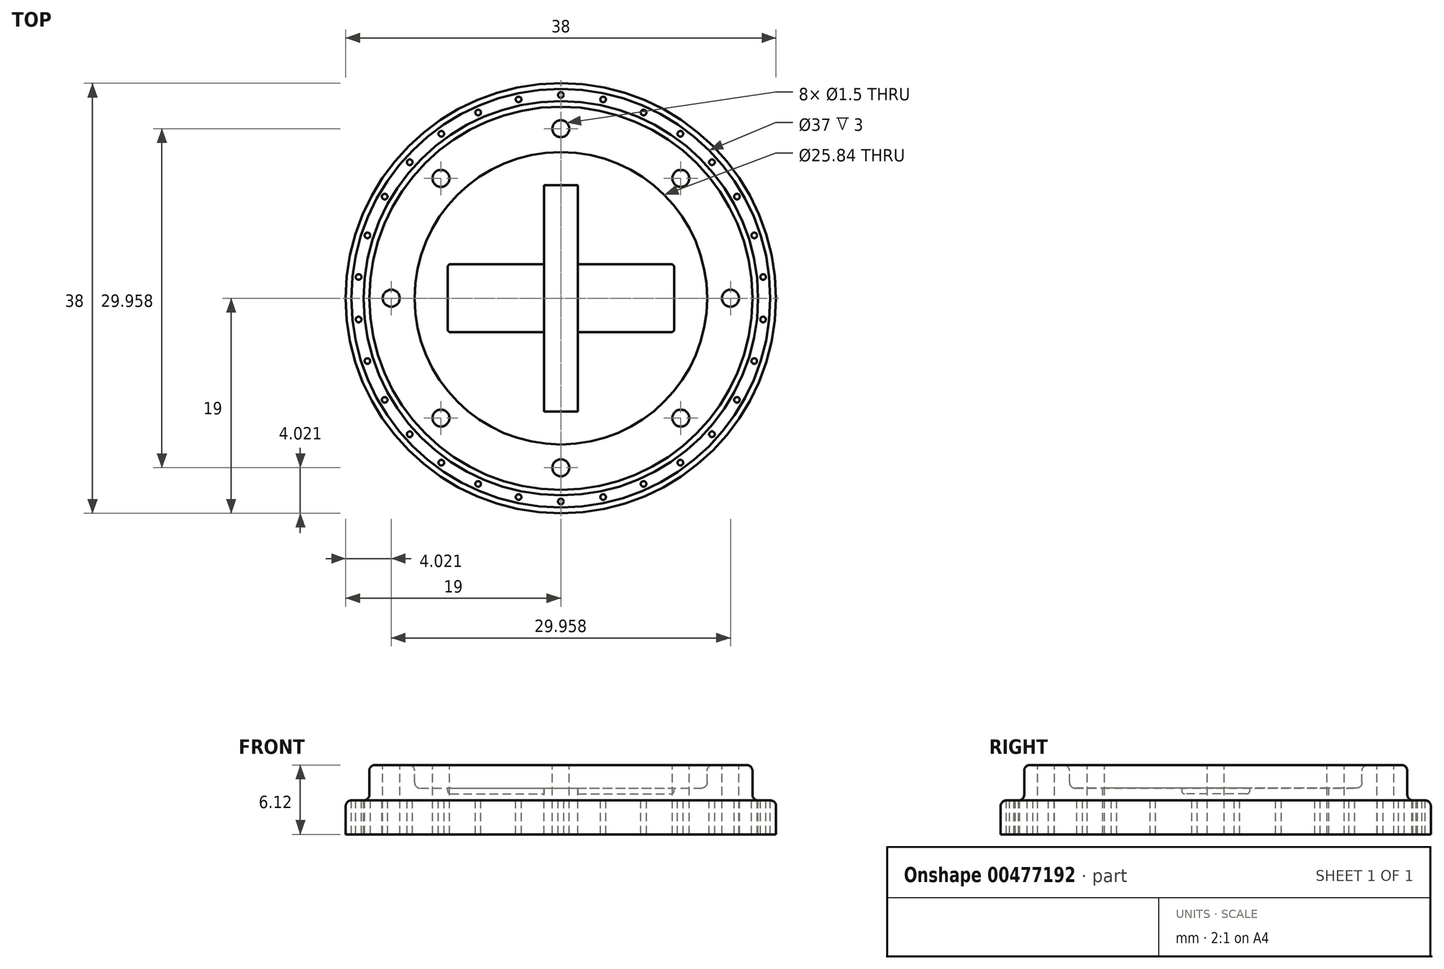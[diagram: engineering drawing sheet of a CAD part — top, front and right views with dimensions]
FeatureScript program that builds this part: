
annotation { "Feature Type Name" : "Feature", "Feature Type Description" : "" }
export const myFeature = defineFeature(function(context is Context, id is Id, definition is map)
    precondition{}
    {
        {
            var Q0;
            Q0=qCreatedBy(makeId("Front.planeOp"),FACE);
            var sketch = newSketch(context, id + "F0", { "sketchPlane" : qUnion([Q0])});
            skLineSegment(sketch, "E0", {"start": v(0, 0) * mm, "end": v(-19, 0) * mm});
            skLineSegment(sketch, "E1", {"start": v(-19, 0) * mm, "end": v(-19, 3) * mm});
            skLineSegment(sketch, "E2", {"start": v(-19, 3) * mm, "end": v(-16.92, 3) * mm});
            skLineSegment(sketch, "E3", {"start": v(-16.92, 3) * mm, "end": v(-16.92, 6.12) * mm});
            skLineSegment(sketch, "E4", {"start": v(-16.92, 6.12) * mm, "end": v(-12.92, 6.12) * mm});
            skLineSegment(sketch, "E5", {"start": v(-12.92, 6.12) * mm, "end": v(-12.92, 4.08) * mm});
            skLineSegment(sketch, "E6", {"start": v(-12.92, 4.08) * mm, "end": v(0, 4.08) * mm});
            skLineSegment(sketch, "E7", {"start": v(0, 4.08) * mm, "end": v(0, 0) * mm});
            skSolve(sketch);
        }
        {
            var Q0;
            Q0 = qSketchRegion(id + "F0", true);
            var Q1;
            Q1=sQuery(id+"F0.wireOp",EDGE,"E7");
            revolve(context, id + "F1", {"entities" : qUnion([Q0]), "axis" : qUnion([Q1]), "revolveType" : RevolveType.FULL});
        }
        {
            var Q0;
            Q0=makeQuery(id+"F1.opRevolve","SWEPT_EDGE",EDGE,{"disambiguationData":[OSD([sQuery(id+"F0.wireOp",EDGE,"E2"),sQuery(id+"F0.wireOp",EDGE,"E3")])]});
            var Q1;
            Q1=makeQuery(id+"F1.opRevolve","SWEPT_EDGE",EDGE,{"disambiguationData":[OSD([sQuery(id+"F0.wireOp",EDGE,"E1"),sQuery(id+"F0.wireOp",EDGE,"E2")])]});
            fillet(context, id + "F2", {"entities" : qUnion([Q0, Q1]), "radius" : 0.5 * mm, "tangentPropagation" : true, "allowEdgeOverflow" : false});
        }
        {
            var Q0;
            Q0=makeQuery(id+"F1.opRevolve","SWEPT_EDGE",EDGE,{"disambiguationData":[OSD([sQuery(id+"F0.wireOp",EDGE,"E3"),sQuery(id+"F0.wireOp",EDGE,"E4")])]});
            var Q1;
            Q1=makeQuery(id+"F1.opRevolve","SWEPT_EDGE",EDGE,{"disambiguationData":[OSD([sQuery(id+"F0.wireOp",EDGE,"E4"),sQuery(id+"F0.wireOp",EDGE,"E5")])]});
            var Q2;
            Q2=makeQuery(id+"F1.opRevolve","SWEPT_EDGE",EDGE,{"disambiguationData":[OSD([sQuery(id+"F0.wireOp",EDGE,"E5"),sQuery(id+"F0.wireOp",EDGE,"E6")])]});
            fillet(context, id + "F3", {"entities" : qUnion([Q0, Q1, Q2]), "radius" : 0.5 * mm, "tangentPropagation" : true, "allowEdgeOverflow" : false});
        }
        {
            var Q0;
            Q0=makeQuery(id+"F1.opRevolve","SWEPT_FACE",FACE,{"disambiguationData":[OSD([sQuery(id+"F0.wireOp",EDGE,"E6")])]});
            var Q1;
            Q1 = qBodyType(qCreatedBy(id + "F5" ,EDGE), BodyType.WIRE);
            cPlane(context, id + "F4", {"entities" : qUnion([Q0, Q1]), "cplaneType" : CPlaneType.OFFSET, "offset" : 0 * mm, "width" : 150 * mm, "height" : 150 * mm});
        }
        {
            var Q0;
            Q0=qCreatedBy(id+"F4.planeOp",FACE);
            var sketch = newSketch(context, id + "F5", { "sketchPlane" : qUnion([Q0])});
            skLineSegment(sketch, "E8.bottom", {"start": v(-10, 3) * mm, "end": v(10, 3) * mm});
            skLineSegment(sketch, "E8.top", {"start": v(-10, -3) * mm, "end": v(10, -3) * mm});
            skLineSegment(sketch, "E8.left", {"start": v(-10, 3) * mm, "end": v(-10, -3) * mm});
            skLineSegment(sketch, "E8.right", {"start": v(10, 3) * mm, "end": v(10, -3) * mm});
            skPoint(sketch, "E8.middle", {"position": v(0, 0) * mm});
            skSolve(sketch);
        }
        {
            var Q0;
            Q0 = qSketchRegion(id + "F5", true);
            extrude(context, id + "F6", {"entities" : qUnion([Q0]), "operationType" : NewBodyOperationType.REMOVE, "oppositeDirection" : true, "depth" : 0.5 * mm});
        }
        {
            var Q0;
            Q0=makeQuery(id+"F6.boolean.opBoolean","COPY",EDGE,{"derivedFrom":makeQuery(id+"F6.opExtrude","SWEPT_EDGE",EDGE,{"disambiguationData":[OSD([sQuery(id+"F5.wireOp",EDGE,"E8.bottom"),sQuery(id+"F5.wireOp",EDGE,"E8.left")])]})});
            var Q1;
            Q1=makeQuery(id+"F6.boolean.opBoolean","COPY",EDGE,{"derivedFrom":makeQuery(id+"F6.opExtrude","SWEPT_EDGE",EDGE,{"disambiguationData":[OSD([sQuery(id+"F5.wireOp",EDGE,"E8.top"),sQuery(id+"F5.wireOp",EDGE,"E8.left")])]})});
            var Q2;
            Q2=makeQuery(id+"F6.boolean.opBoolean","COPY",EDGE,{"derivedFrom":makeQuery(id+"F6.opExtrude","SWEPT_EDGE",EDGE,{"disambiguationData":[OSD([sQuery(id+"F5.wireOp",EDGE,"E8.bottom"),sQuery(id+"F5.wireOp",EDGE,"E8.right")])]})});
            var Q3;
            Q3=makeQuery(id+"F6.boolean.opBoolean","COPY",EDGE,{"derivedFrom":makeQuery(id+"F6.opExtrude","SWEPT_EDGE",EDGE,{"disambiguationData":[OSD([sQuery(id+"F5.wireOp",EDGE,"E8.top"),sQuery(id+"F5.wireOp",EDGE,"E8.right")])]})});
            var Q4;
            Q4=makeQuery(id+"F6.boolean.opBoolean","COPY",EDGE,{"derivedFrom":makeQuery(id+"F6.opExtrude","CAP_EDGE",EDGE,{"disambiguationData":[OSD([sQuery(id+"F5.wireOp",EDGE,"E8.right")])],"isStart":false})});
            var Q5;
            Q5=makeQuery(id+"F6.boolean.opBoolean","COPY",EDGE,{"derivedFrom":makeQuery(id+"F6.opExtrude","CAP_EDGE",EDGE,{"disambiguationData":[OSD([sQuery(id+"F5.wireOp",EDGE,"E8.top")])],"isStart":false})});
            var Q6;
            Q6=makeQuery(id+"F6.boolean.opBoolean","COPY",EDGE,{"derivedFrom":makeQuery(id+"F6.opExtrude","CAP_EDGE",EDGE,{"disambiguationData":[OSD([sQuery(id+"F5.wireOp",EDGE,"E8.bottom")])],"isStart":false})});
            var Q7;
            Q7=makeQuery(id+"F6.boolean.opBoolean","COPY",EDGE,{"derivedFrom":makeQuery(id+"F6.opExtrude","CAP_EDGE",EDGE,{"disambiguationData":[OSD([sQuery(id+"F5.wireOp",EDGE,"E8.left")])],"isStart":false})});
            fillet(context, id + "F7", {"entities" : qUnion([Q0, Q1, Q2, Q3, Q4, Q5, Q6, Q7]), "radius" : 0.25 * mm, "tangentPropagation" : true, "allowEdgeOverflow" : false});
        }
        {
            var Q0;
            Q0=qCreatedBy(id+"F4.planeOp",FACE);
            var sketch = newSketch(context, id + "F8", { "sketchPlane" : qUnion([Q0])});
            skLineSegment(sketch, "E9.bottom", {"start": v(-1.5, 10) * mm, "end": v(1.5, 10) * mm});
            skLineSegment(sketch, "E9.top", {"start": v(-1.5, -10) * mm, "end": v(1.5, -10) * mm});
            skLineSegment(sketch, "E9.left", {"start": v(-1.5, 10) * mm, "end": v(-1.5, -10) * mm});
            skLineSegment(sketch, "E9.right", {"start": v(1.5, 10) * mm, "end": v(1.5, -10) * mm});
            skPoint(sketch, "E9.middle", {"position": v(0, 0) * mm});
            skSolve(sketch);
        }
        {
            var Q0;
            Q0 = qSketchRegion(id + "F8", true);
            extrude(context, id + "F9", {"entities" : qUnion([Q0]), "operationType" : NewBodyOperationType.REMOVE, "oppositeDirection" : true, "depth" : 5 * mm});
        }
        {
            var Q0;
            Q0=makeQuery(id+"F1.opRevolve","SWEPT_FACE",FACE,{"disambiguationData":[OSD([sQuery(id+"F0.wireOp",EDGE,"E4")])]});
            var sketch = newSketch(context, id + "F10", { "sketchPlane" : qUnion([Q0])});
            skCircle(sketch, "E10", {"center": v(0, 0) * mm, "radius": 0.75 * mm});
            skCircle(sketch, "E11", {"center": v(0, 0) * mm, "radius": 14.98 * mm, "construction": true});
            skCircle(sketch, "E12", {"center": v(0, 14.98) * mm, "radius": 0.75 * mm});
            skCircle(sketch, "E13.1.0", {"center": v(-10.6, 10.6) * mm, "radius": 0.75 * mm});
            skCircle(sketch, "E13.2.0", {"center": v(-14.98, 0) * mm, "radius": 0.75 * mm});
            skCircle(sketch, "E14.1.3.0", {"center": v(-10.6, -10.6) * mm, "radius": 0.75 * mm});
            skCircle(sketch, "E14.1.4.0", {"center": v(0, -14.98) * mm, "radius": 0.75 * mm});
            skCircle(sketch, "E14.1.5.0", {"center": v(10.6, -10.6) * mm, "radius": 0.75 * mm});
            skCircle(sketch, "E14.1.6.0", {"center": v(14.98, 0) * mm, "radius": 0.75 * mm});
            skCircle(sketch, "E15.1.7.0", {"center": v(10.6, 10.6) * mm, "radius": 0.75 * mm});
            skSolve(sketch);
        }
        {
            var Q0;
            Q0=makeQuery(id+"F10.imprint","IMPRINT",FACE,{"disambiguationData":[TD([[makeQuery(id+"F10.imprint","IMPRINT",EDGE,{"derivedFrom":sQuery(id+"F10.wireOp",EDGE,"E13.1.0")}),1.0]])]});
            var Q1;
            Q1=makeQuery(id+"F10.imprint","IMPRINT",FACE,{"disambiguationData":[TD([[makeQuery(id+"F10.imprint","IMPRINT",EDGE,{"derivedFrom":sQuery(id+"F10.wireOp",EDGE,"E14.1.3.0")}),1.0]])]});
            var Q2;
            Q2=makeQuery(id+"F10.imprint","IMPRINT",FACE,{"disambiguationData":[TD([[makeQuery(id+"F10.imprint","IMPRINT",EDGE,{"derivedFrom":sQuery(id+"F10.wireOp",EDGE,"E13.2.0")}),1.0]])]});
            var Q3;
            Q3=makeQuery(id+"F10.imprint","IMPRINT",FACE,{"disambiguationData":[TD([[makeQuery(id+"F10.imprint","IMPRINT",EDGE,{"derivedFrom":sQuery(id+"F10.wireOp",EDGE,"E12")}),1.0]])]});
            var Q4;
            Q4=makeQuery(id+"F10.imprint","IMPRINT",FACE,{"disambiguationData":[TD([[makeQuery(id+"F10.imprint","IMPRINT",EDGE,{"derivedFrom":sQuery(id+"F10.wireOp",EDGE,"E14.1.4.0")}),1.0]])]});
            var Q5;
            Q5=makeQuery(id+"F10.imprint","IMPRINT",FACE,{"disambiguationData":[TD([[makeQuery(id+"F10.imprint","IMPRINT",EDGE,{"derivedFrom":sQuery(id+"F10.wireOp",EDGE,"E14.1.5.0")}),1.0]])]});
            var Q6;
            Q6=makeQuery(id+"F10.imprint","IMPRINT",FACE,{"disambiguationData":[TD([[makeQuery(id+"F10.imprint","IMPRINT",EDGE,{"derivedFrom":sQuery(id+"F10.wireOp",EDGE,"E14.1.6.0")}),1.0]])]});
            var Q7;
            Q7=makeQuery(id+"F10.imprint","IMPRINT",FACE,{"disambiguationData":[TD([[makeQuery(id+"F10.imprint","IMPRINT",EDGE,{"derivedFrom":sQuery(id+"F10.wireOp",EDGE,"E15.1.7.0")}),1.0]])]});
            extrude(context, id + "F11", {"entities" : qUnion([Q0, Q1, Q2, Q3, Q4, Q5, Q6, Q7]), "operationType" : NewBodyOperationType.REMOVE, "oppositeDirection" : true, "depth" : 25 * mm});
        }
        {
            var Q0;
            Q0=makeQuery(id+"F1.opRevolve","SWEPT_FACE",FACE,{"disambiguationData":[OSD([sQuery(id+"F0.wireOp",EDGE,"E2")])]});
            var sketch = newSketch(context, id + "F12", { "sketchPlane" : qUnion([Q0])});
            skCircle(sketch, "E16", {"center": v(0, 0) * mm, "radius": 17.96 * mm, "construction": true});
            skCircle(sketch, "E17", {"center": v(0, 17.96) * mm, "radius": 0.25 * mm});
            skCircle(sketch, "E18.1.1", {"center": v(-3.73, 17.57) * mm, "radius": 0.25 * mm});
            skCircle(sketch, "E18.2.1", {"center": v(-7.3, 16.4) * mm, "radius": 0.25 * mm});
            skCircle(sketch, "E18.3.1", {"center": v(-10.56, 14.53) * mm, "radius": 0.25 * mm});
            skCircle(sketch, "E18.4.1", {"center": v(-13.35, 12.02) * mm, "radius": 0.25 * mm});
            skCircle(sketch, "E18.5.1", {"center": v(-15.55, 8.98) * mm, "radius": 0.25 * mm});
            skCircle(sketch, "E18.6.1", {"center": v(-17.08, 5.55) * mm, "radius": 0.25 * mm});
            skCircle(sketch, "E18.7.1", {"center": v(-17.86, 1.88) * mm, "radius": 0.25 * mm});
            skCircle(sketch, "E18.8.1", {"center": v(-17.86, -1.88) * mm, "radius": 0.25 * mm});
            skCircle(sketch, "E18.9.1", {"center": v(-17.08, -5.55) * mm, "radius": 0.25 * mm});
            skCircle(sketch, "E18.10.1", {"center": v(-15.55, -8.98) * mm, "radius": 0.25 * mm});
            skCircle(sketch, "E18.11.1", {"center": v(-13.35, -12.02) * mm, "radius": 0.25 * mm});
            skCircle(sketch, "E18.12.1", {"center": v(-10.56, -14.53) * mm, "radius": 0.25 * mm});
            skCircle(sketch, "E18.13.1", {"center": v(-7.3, -16.4) * mm, "radius": 0.25 * mm});
            skCircle(sketch, "E18.14.1", {"center": v(-3.73, -17.57) * mm, "radius": 0.25 * mm});
            skCircle(sketch, "E18.15.1", {"center": v(0, -17.96) * mm, "radius": 0.25 * mm});
            skCircle(sketch, "E18.16.1", {"center": v(3.73, -17.57) * mm, "radius": 0.25 * mm});
            skCircle(sketch, "E18.17.1", {"center": v(7.3, -16.4) * mm, "radius": 0.25 * mm});
            skCircle(sketch, "E18.18.1", {"center": v(10.56, -14.53) * mm, "radius": 0.25 * mm});
            skCircle(sketch, "E18.19.1", {"center": v(13.35, -12.02) * mm, "radius": 0.25 * mm});
            skCircle(sketch, "E18.20.1", {"center": v(15.55, -8.98) * mm, "radius": 0.25 * mm});
            skCircle(sketch, "E18.21.1", {"center": v(17.08, -5.55) * mm, "radius": 0.25 * mm});
            skCircle(sketch, "E18.22.1", {"center": v(17.86, -1.88) * mm, "radius": 0.25 * mm});
            skCircle(sketch, "E18.23.1", {"center": v(17.86, 1.88) * mm, "radius": 0.25 * mm});
            skCircle(sketch, "E18.24.1", {"center": v(17.08, 5.55) * mm, "radius": 0.25 * mm});
            skCircle(sketch, "E18.25.1", {"center": v(15.55, 8.98) * mm, "radius": 0.25 * mm});
            skCircle(sketch, "E18.26.1", {"center": v(13.35, 12.02) * mm, "radius": 0.25 * mm});
            skCircle(sketch, "E18.27.1", {"center": v(10.56, 14.53) * mm, "radius": 0.25 * mm});
            skCircle(sketch, "E18.28.1", {"center": v(7.3, 16.4) * mm, "radius": 0.25 * mm});
            skCircle(sketch, "E18.29.1", {"center": v(3.73, 17.57) * mm, "radius": 0.25 * mm});
            skSolve(sketch);
        }
        {
            var Q0;
            Q0=makeQuery(id+"F12.imprint","IMPRINT",FACE,{"disambiguationData":[TD([[makeQuery(id+"F12.imprint","IMPRINT",EDGE,{"derivedFrom":sQuery(id+"F12.wireOp",EDGE,"E17")}),-1.0]])]});
            extrude(context, id + "F13", {"entities" : qUnion([Q0]), "operationType" : NewBodyOperationType.REMOVE, "oppositeDirection" : true, "depth" : 25 * mm});
        }
    });
